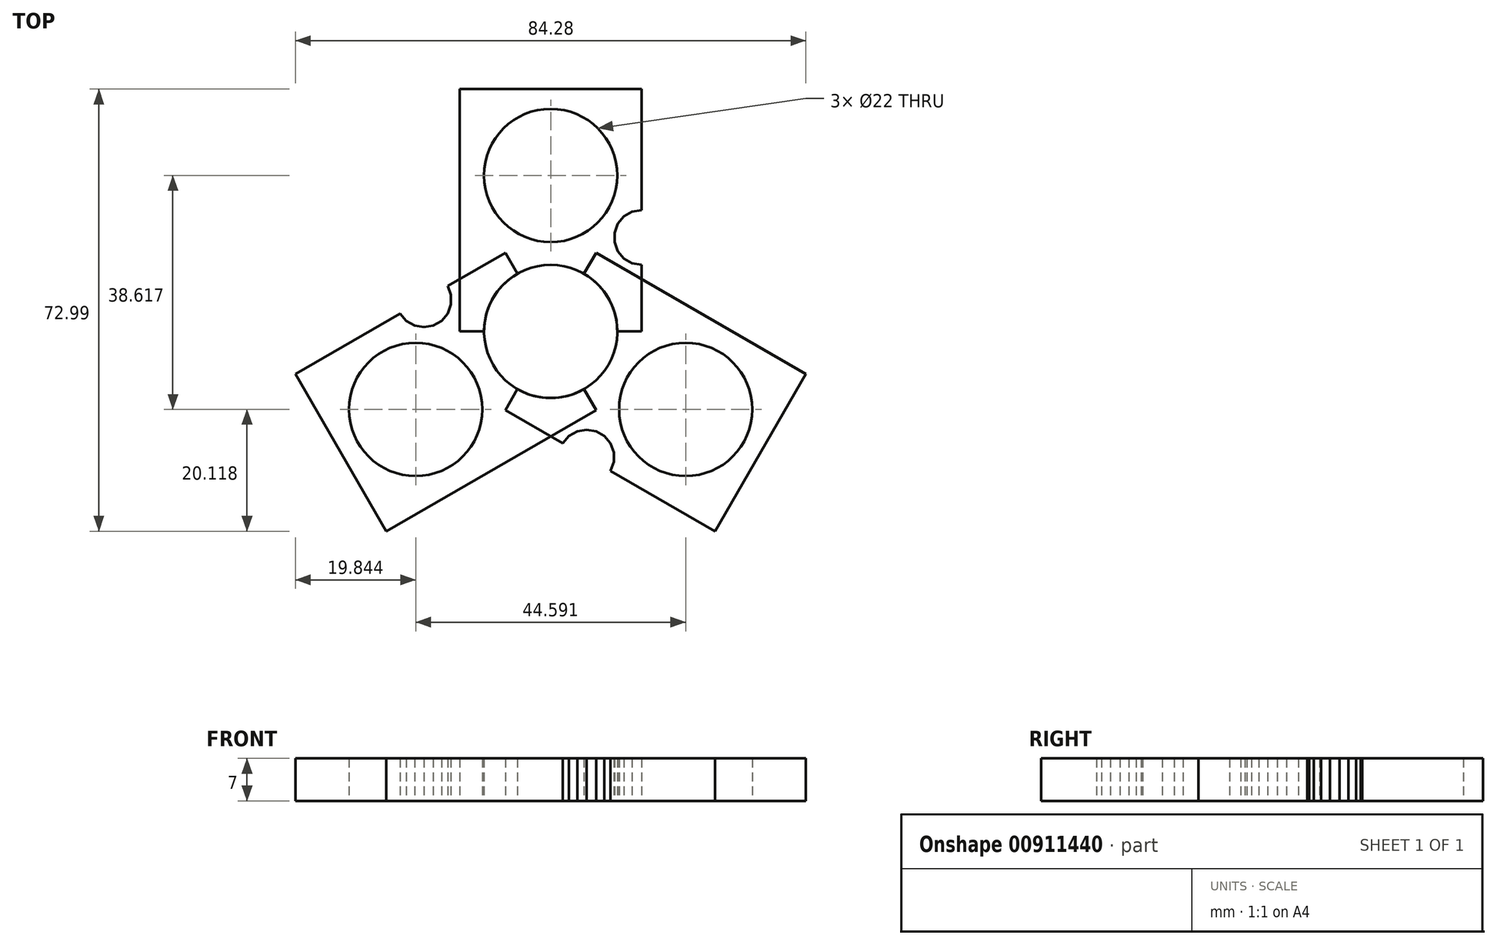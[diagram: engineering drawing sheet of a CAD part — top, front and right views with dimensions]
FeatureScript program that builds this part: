
annotation { "Feature Type Name" : "Feature", "Feature Type Description" : "" }
export const myFeature = defineFeature(function(context is Context, id is Id, definition is map)
    precondition{}
    {
        {
            var Q0;
            Q0=qCreatedBy(makeId("Top.planeOp"),FACE);
            var sketch = newSketch(context, id + "F0", { "sketchPlane" : qUnion([Q0])});
            skCircle(sketch, "E0", {"center": v(0, 0) * mm, "radius": 11 * mm});
            skLineSegment(sketch, "E1.bottom", {"start": v(0, 0) * mm, "end": v(15, 0) * mm});
            skLineSegment(sketch, "E1.top", {"start": v(0, 40) * mm, "end": v(15, 40) * mm});
            skLineSegment(sketch, "E1.left", {"start": v(0, 0) * mm, "end": v(0, 40) * mm});
            skLineSegment(sketch, "E1.right", {"start": v(15, 0) * mm, "end": v(15, 40) * mm});
            skLineSegment(sketch, "E2.bottom", {"start": v(0, 0) * mm, "end": v(-15, 0) * mm});
            skLineSegment(sketch, "E2.top", {"start": v(0, 40) * mm, "end": v(-15, 40) * mm});
            skLineSegment(sketch, "E2.right", {"start": v(-15, 0) * mm, "end": v(-15, 40) * mm});
            skLineSegment(sketch, "E3", {"start": v(0, 40) * mm, "end": v(0, 25.74) * mm});
            skCircle(sketch, "E4", {"center": v(0, 25.74) * mm, "radius": 11 * mm});
            skCircle(sketch, "E5.cCircle", {"center": v(15, 15.51) * mm, "radius": 4.54 * mm, "construction": true});
            skLineSegment(sketch, "E5.0", {"start": v(15, 10.98) * mm, "end": v(13.45, 11.25) * mm});
            skLineSegment(sketch, "E5.1", {"start": v(13.45, 11.25) * mm, "end": v(12.08, 12.04) * mm});
            skLineSegment(sketch, "E5.2", {"start": v(12.08, 12.04) * mm, "end": v(11.07, 13.25) * mm});
            skLineSegment(sketch, "E5.3", {"start": v(11.07, 13.25) * mm, "end": v(10.53, 14.73) * mm});
            skLineSegment(sketch, "E5.4", {"start": v(10.53, 14.73) * mm, "end": v(10.53, 16.3) * mm});
            skLineSegment(sketch, "E5.5", {"start": v(10.53, 16.3) * mm, "end": v(11.07, 17.78) * mm});
            skLineSegment(sketch, "E5.6", {"start": v(11.07, 17.78) * mm, "end": v(12.08, 18.99) * mm});
            skLineSegment(sketch, "E5.7", {"start": v(12.08, 18.99) * mm, "end": v(13.45, 19.78) * mm});
            skLineSegment(sketch, "E5.8", {"start": v(13.45, 19.78) * mm, "end": v(15, 20.05) * mm});
            skLineSegment(sketch, "E5.9", {"start": v(15, 20.05) * mm, "end": v(16.55, 19.78) * mm});
            skLineSegment(sketch, "E5.10", {"start": v(16.55, 19.78) * mm, "end": v(17.92, 18.99) * mm});
            skLineSegment(sketch, "E5.11", {"start": v(17.92, 18.99) * mm, "end": v(18.93, 17.78) * mm});
            skLineSegment(sketch, "E5.12", {"start": v(18.93, 17.78) * mm, "end": v(19.47, 16.3) * mm});
            skLineSegment(sketch, "E5.13", {"start": v(19.47, 16.3) * mm, "end": v(19.47, 14.73) * mm});
            skLineSegment(sketch, "E5.14", {"start": v(19.47, 14.73) * mm, "end": v(18.93, 13.25) * mm});
            skLineSegment(sketch, "E5.15", {"start": v(18.93, 13.25) * mm, "end": v(17.92, 12.04) * mm});
            skLineSegment(sketch, "E5.16", {"start": v(17.92, 12.04) * mm, "end": v(16.55, 11.25) * mm});
            skLineSegment(sketch, "E5.17", {"start": v(16.55, 11.25) * mm, "end": v(15, 10.98) * mm});
            skSolve(sketch);
        }
        {
            var Q0;
            {var subQ9=sQuery(id+"F0.wireOp",EDGE,"E1.top");Q0=makeQuery(id+"F0.imprint","IMPRINT",FACE,{"disambiguationData":[TD([[makeQuery(id+"F0.imprint","IMPRINT",EDGE,{"derivedFrom":subQ9}),-1.0]])]});}
            var Q1;
            {var subQ0=sQuery(id+"F0.wireOp",EDGE,"E2.top");Q1=makeQuery(id+"F0.imprint","IMPRINT",FACE,{"disambiguationData":[TD([[makeQuery(id+"F0.imprint","IMPRINT",EDGE,{"derivedFrom":subQ0}),1.0]])]});}
            extrude(context, id + "F1", {"entities" : qUnion([Q0, Q1]), "depth" : 7 * mm, "offsetDistance" : 25 * mm});
        }
        {
            var Q0;
            Q0=qCreatedBy(makeId("Front.planeOp"),FACE);
            var sketch = newSketch(context, id + "F2", { "sketchPlane" : qUnion([Q0])});
            skLineSegment(sketch, "E6", {"start": v(0, 0) * mm, "end": v(0, 47.27) * mm});
            skSolve(sketch);
        }
        {
            var Q0;
            Q0=makeQuery(id+"F1.opExtrude","SWEPT_BODY",BODY,{"disambiguationData":[OSD([sQuery(id+"F0.wireOp",EDGE,"E0"),sQuery(id+"F0.wireOp",EDGE,"E1.bottom"),sQuery(id+"F0.wireOp",EDGE,"E1.top"),sQuery(id+"F0.wireOp",EDGE,"E1.right"),sQuery(id+"F0.wireOp",EDGE,"E2.bottom"),sQuery(id+"F0.wireOp",EDGE,"E2.top"),sQuery(id+"F0.wireOp",EDGE,"E2.right"),sQuery(id+"F0.wireOp",EDGE,"E4")])]});
            var Q1;
            Q1=sQuery(id+"F2.wireOp",EDGE,"E6");
            transform(context, id + "F3", {"entities" : qUnion([Q0]), "transformType" : TransformType.ROTATION, "transformAxis" : qUnion([Q1]), "angle" : 120 * degree, "makeCopy" : true});
        }
        {
            var Q0;
            Q0=makeQuery(id+"F1.opExtrude","SWEPT_BODY",BODY,{"disambiguationData":[OSD([sQuery(id+"F0.wireOp",EDGE,"E0"),sQuery(id+"F0.wireOp",EDGE,"E1.bottom"),sQuery(id+"F0.wireOp",EDGE,"E1.top"),sQuery(id+"F0.wireOp",EDGE,"E1.right"),sQuery(id+"F0.wireOp",EDGE,"E2.bottom"),sQuery(id+"F0.wireOp",EDGE,"E2.top"),sQuery(id+"F0.wireOp",EDGE,"E2.right"),sQuery(id+"F0.wireOp",EDGE,"E4")])]});
            var Q1;
            Q1=sQuery(id+"F2.wireOp",EDGE,"E6");
            transform(context, id + "F4", {"entities" : qUnion([Q0]), "transformType" : TransformType.ROTATION, "transformAxis" : qUnion([Q1]), "angle" : 240 * degree, "makeCopy" : true});
        }
    });
